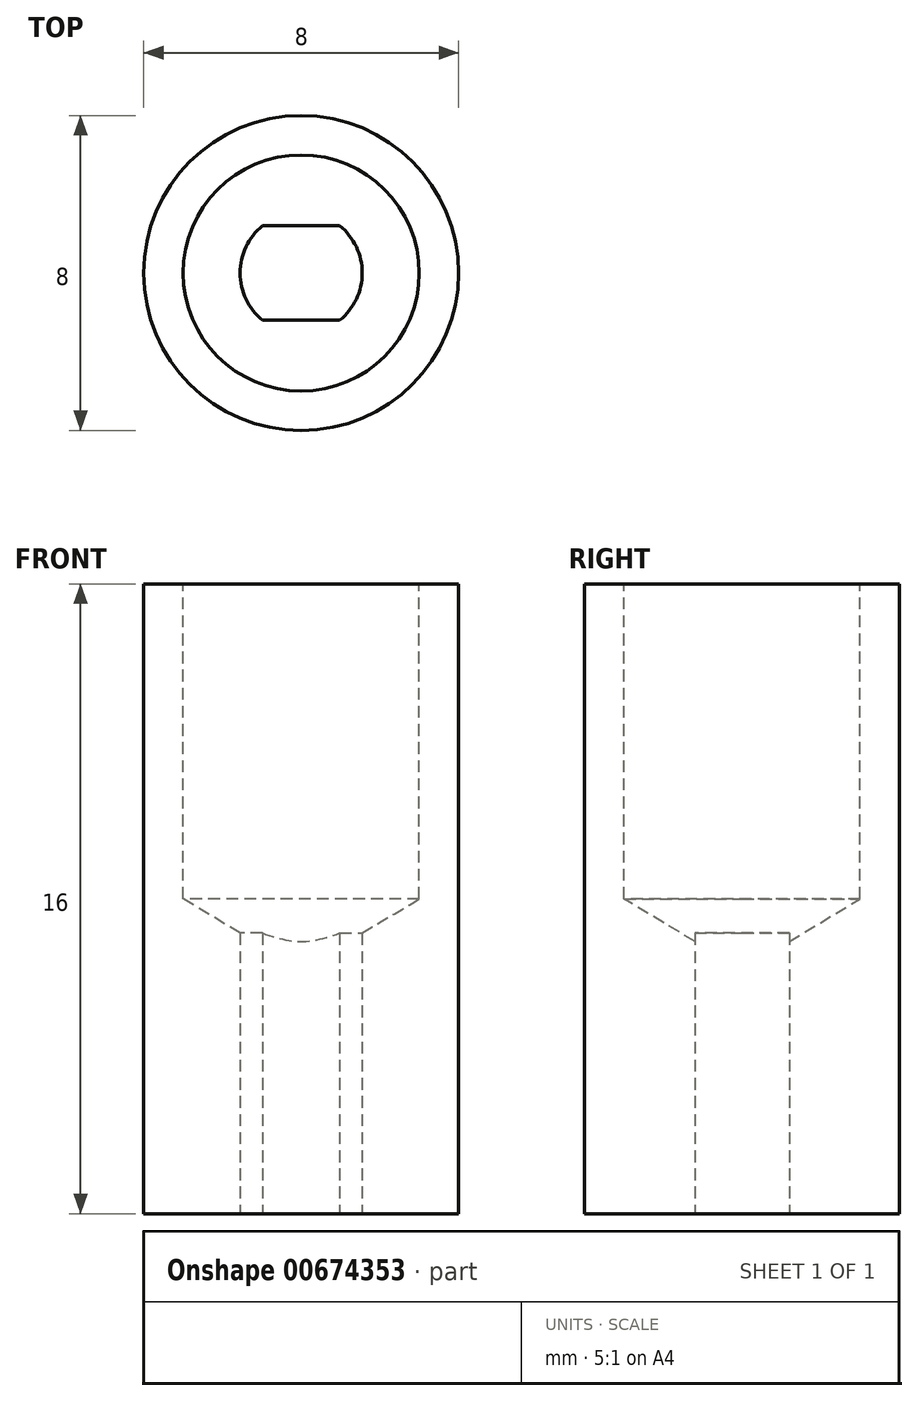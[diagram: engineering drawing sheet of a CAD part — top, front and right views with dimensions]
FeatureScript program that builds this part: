
annotation { "Feature Type Name" : "Feature", "Feature Type Description" : "" }
export const myFeature = defineFeature(function(context is Context, id is Id, definition is map)
    precondition{}
    {
        {
            var Q0;
            Q0=qCreatedBy(makeId("Top.planeOp"),FACE);
            var sketch = newSketch(context, id + "F0", { "sketchPlane" : qUnion([Q0])});
            skArc(sketch, "E0", {"start": v(-0.98, 1.2) * mm, "mid": v(-1.4, 0.66) * mm, "end": v(-1.55, 0) * mm});
            skLineSegment(sketch, "E1", {"start": v(-1.55, 0) * mm, "end": v(1.55, 0) * mm, "construction": true});
            skLineSegment(sketch, "E2", {"start": v(-0.98, 1.2) * mm, "end": v(0.98, 1.2) * mm});
            skArc(sketch, "E3.trimOffspring", {"start": v(1.55, 0) * mm, "mid": v(1.4, 0.66) * mm, "end": v(0.98, 1.2) * mm});
            skArc(sketch, "E4.MirrorCS", {"start": v(-0.98, -1.2) * mm, "mid": v(-1.4, -0.66) * mm, "end": v(-1.55, 0) * mm});
            skLineSegment(sketch, "E5.MirrorCS", {"start": v(-0.98, -1.2) * mm, "end": v(0.98, -1.2) * mm});
            skArc(sketch, "E6.MirrorCS", {"start": v(1.55, 0) * mm, "mid": v(1.4, -0.66) * mm, "end": v(0.98, -1.2) * mm});
            skCircle(sketch, "E7", {"center": v(0, 0) * mm, "radius": 4 * mm});
            skSolve(sketch);
        }
        {
            var Q0;
            Q0 = qSketchRegion(id + "F0", true);
            extrude(context, id + "F1", {"entities" : qUnion([Q0]), "depth" : 16 * mm, "offsetDistance" : 25 * mm});
        }
        {
            var Q0;
            Q0=makeQuery(id+"F1.opExtrude","CAP_FACE",FACE,{"disambiguationData":[OSD([sQuery(id+"F0.wireOp",EDGE,"E0"),sQuery(id+"F0.wireOp",EDGE,"E2"),sQuery(id+"F0.wireOp",EDGE,"E3.trimOffspring"),sQuery(id+"F0.wireOp",EDGE,"E4.MirrorCS"),sQuery(id+"F0.wireOp",EDGE,"E5.MirrorCS"),sQuery(id+"F0.wireOp",EDGE,"E6.MirrorCS"),sQuery(id+"F0.wireOp",EDGE,"E7")])],"isStart":false});
            var sketch = newSketch(context, id + "F2", { "sketchPlane" : qUnion([Q0])});
            skCircle(sketch, "E8", {"center": v(0, 0) * mm, "radius": 3 * mm});
            skSolve(sketch);
        }
        {
            var Q0;
            Q0=sQuery(id+"F2.wireOp",VERTEX,"E8.center");
            var Q1;
            Q1=makeQuery(id+"F1.opExtrude","SWEPT_BODY",BODY,{"disambiguationData":[OSD([sQuery(id+"F0.wireOp",EDGE,"E0"),sQuery(id+"F0.wireOp",EDGE,"E2"),sQuery(id+"F0.wireOp",EDGE,"E3.trimOffspring"),sQuery(id+"F0.wireOp",EDGE,"E4.MirrorCS"),sQuery(id+"F0.wireOp",EDGE,"E5.MirrorCS"),sQuery(id+"F0.wireOp",EDGE,"E6.MirrorCS"),sQuery(id+"F0.wireOp",EDGE,"E7")])]});
            hole(context, id + "F3", {"style" : HoleStyle.SIMPLE, "endStyle" : HoleEndStyle.BLIND, "holeDiameter" : 6 * mm, "majorDiameter" : 5 * mm, "holeDepth" : 8 * mm, "isTappedThrough" : true, "tappedDepth" : 12 * mm, "tapClearance" : 3, "locations" : qUnion([Q0]), "scope" : qUnion([Q1])});
        }
    });
